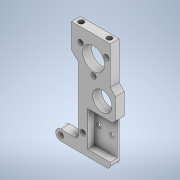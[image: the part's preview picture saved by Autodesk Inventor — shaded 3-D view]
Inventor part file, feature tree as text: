
AUTODESK INVENTOR PART (.ipt)
format: ipt  version: 2020.2 (Build 242310000, 310)  size: 248,320 bytes
history: native  units: mm
features: extrude x4, sketch x4, fillet x2, thread x2, projected_geometry x1
ambient origin geometry x8: Origin, YZ Plane, XZ Plane, XY Plane, X Axis, Y Axis, Z Axis, Center Point
bodies: Solid1 (feature_tree)
feature tree (13):
  extrude  "Extrusion1"  Depth=6.0mm
  fillet  "Fillet1"  Radius=28.0mm
  fillet  "Fillet2"  Radius=6.0mm
  extrude  "Extrusion2"  Depth=3.0mm
  extrude  "Extrusion3"  Depth=56.0mm
  thread  "Thread1"  [1 undecoded]
  thread  "Thread2"  [1 undecoded]
  extrude  "Extrusion4"  Depth=3.0mm
  sketch  "Sketch1"  dims[d0=3.0mm d1=6.0mm d2=28.0mm d3=6.0mm]
  sketch  "Sketch2"  dims[d4=0.0mm d5=3.0mm]
  sketch  "Sketch3"  dims[d6=18.0mm d7=56.0mm d8=11.0mm d9=4.5mm]
  projected_geometry  "Projected Loop1"
  sketch  "Sketch5"  dims[d10=25.5mm d11=12.5mm d12=19.15mm d14=1.6mm d17=12.0mm d18=30.0mm d20=360.0deg d22=4.0mm d23=14.0mm d24=45.0deg d25=3.0mm d26=12.0mm d27=6.0mm d28=135.0deg d29=135.0deg d30=5.0mm d31=0.0mm d32=3.0mm d33=10.5mm d34=2.5mm d35=2.5mm d36=14.5mm d37=7.5mm d38=2.5mm d39=15.0mm d40=13.5mm d41=2.0mm d42=2.0mm d43=12.75mm d44=20.0mm d45=23.75mm d46=4.0mm d47=0.0mm d48=3.0mm d49=3.0mm d50=2.5mm d51=2.5mm d52=3.0mm d53=3.0mm d54=6.0mm d55=0.0mm d56=7.0mm d57=0.0mm d58=7.0mm d59=0.0mm d60=8.5mm d61=270.0deg d62=3.0mm d63=3.0mm d64=3.0mm d65=3.0mm d66=0.0mm]
note: 2 required parameter values undecoded (feature->parameter linkage not recoverable at this tier; creation-order binding heuristic only, values carry confidence <= 0.55)
